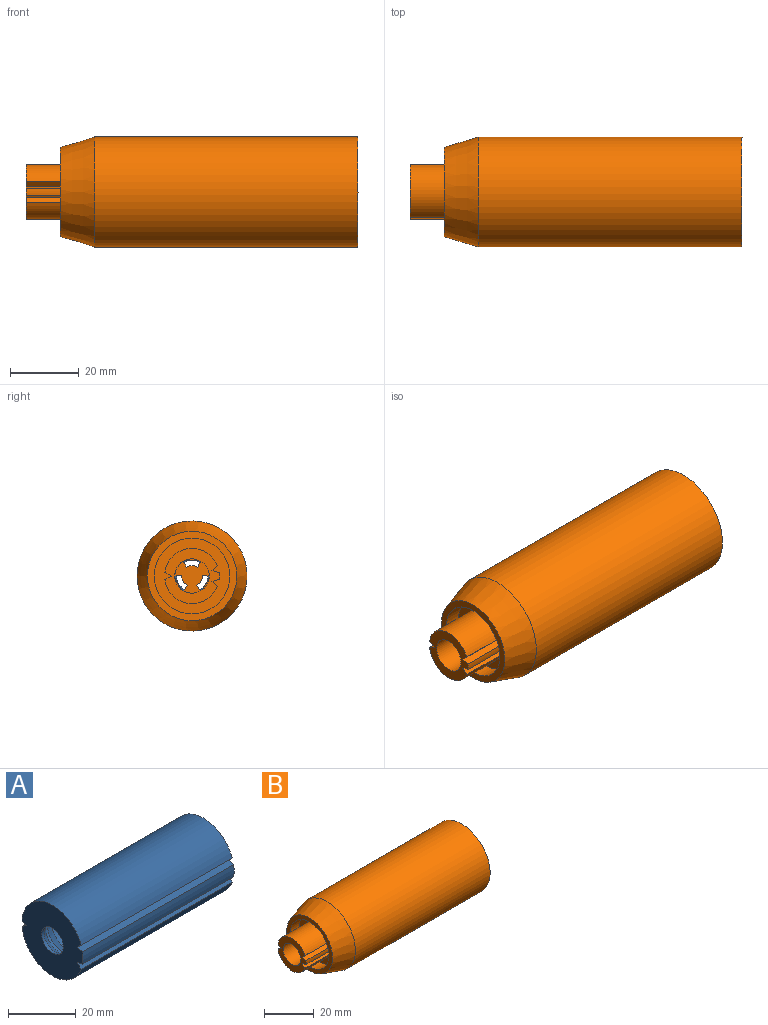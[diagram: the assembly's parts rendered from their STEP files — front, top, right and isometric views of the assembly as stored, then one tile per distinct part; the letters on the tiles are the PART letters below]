
ASSEMBLY  parts=2 mates=1
PART A: 27 faces, bbox 63x25.5x25.5 mm
  f0: cylinder r=9.75mm len=54.43mm, axis (-1,0,0), area 3310.2mm2, adj f3,f4,f18,f19,f20,f21,f22,f23
  f1: cylinder r=12.75mm len=63mm, axis (-1,0,0), area 2171.1mm2, adj f3,f9,f11,f15
  f2: cylinder r=12.75mm len=63mm, axis (-1,0,0), area 2171.1mm2, adj f3,f9,f14,f16
  f3: plane 25.5x25.45mm, normal (1,0,0), area 205.2mm2, adj f0,f1,f2,f10,f11,f12,f13,f14
  f4: cone r=7.25mm half-angle=35deg, axis (1,0,0), area 232.8mm2, adj f0,f5
  f5: cylinder r=7.25mm len=14.5mm, axis (-1,0,0), area 91.1mm2, adj f4,f6
  f6: plane 14.5x14.5mm, normal (1,0,0), area 55.8mm2, adj f5,f7
  f7: cone r=4.5mm half-angle=35deg, axis (1,0,0), area 79.8mm2, adj f6,f8
  f8: cylinder r=4.5mm len=9mm, axis (-1,0,0), area 28.3mm2, adj f7,f9
  f9: plane 25.5x25.45mm, normal (-1,0,0), area 440.3mm2, adj f1,f2,f8,f10,f11,f12,f13,f14
  f10: cylinder r=12.75mm len=63mm, axis (-1,0,0), area 278.5mm2, adj f3,f9,f12,f13
  f11: plane 63x1.59mm, normal (0,-0.71,-0.71), area 141.9mm2, adj f1,f3,f9,f12
  f12: plane 63x2.18mm, normal (0,-0.26,0.97), area 141.9mm2, adj f3,f9,f10,f11
  f13: plane 63x2.18mm, normal (0,-0.26,-0.97), area 141.9mm2, adj f3,f9,f10,f14
  f14: plane 63x1.59mm, normal (0,-0.71,0.71), area 141.9mm2, adj f2,f3,f9,f13
  f15: plane 63x1.95mm, normal (0,0.5,-0.87), area 141.9mm2, adj f1,f3,f9,f16
  f16: plane 63x1.95mm, normal (0,0.5,0.87), area 141.9mm2, adj f2,f3,f9,f15
  f17: plane 4x3mm, normal (0,0,-1), area 12mm2, adj f18,f19,f20,f21
  f18: plane 4x1.21mm, normal (-1,0,0), area 4.3mm2, adj f0,f17,f19,f21
  f19: plane 3x1.21mm, normal (0,1,0), area 3.6mm2, adj f0,f17,f18,f20
  f20: plane 4x1.21mm, normal (1,0,0), area 4.3mm2, adj f0,f17,f19,f21
  f21: plane 3x1.21mm, normal (0,-1,0), area 3.6mm2, adj f0,f17,f18,f20
  f22: plane 3x1.21mm, normal (0,-1,0), area 3.6mm2, adj f0,f23,f25,f26
  f23: plane 4x1.21mm, normal (1,0,0), area 4.3mm2, adj f0,f22,f24,f26
  f24: plane 3x1.21mm, normal (0,1,0), area 3.6mm2, adj f0,f23,f25,f26
  f25: plane 4x1.21mm, normal (-1,0,0), area 4.3mm2, adj f0,f22,f24,f26
  f26: plane 4x3mm, normal (0,0,1), area 12mm2, adj f22,f23,f24,f25
PART B: 52 faces, bbox 96.5x32x32 mm
  f0: plane 16x15.92mm, normal (-1,0,0), area 115.8mm2, adj f1,f2,f3,f15,f46,f47,f48,f49
  f1: cylinder r=8mm len=15.29mm, axis (1,0,0), area 312.2mm2, adj f0,f16,f49,f51
  f2: cylinder r=8mm len=15mm, axis (1,0,0), area 29.4mm2, adj f0,f16,f47,f48
  f3: cylinder r=8mm len=15.29mm, axis (1,0,0), area 312.2mm2, adj f0,f16,f46,f50
  f4: plane 26x25.95mm, normal (1,0,0), area 240.6mm2, adj f5,f6,f7,f12,f40,f41,f42,f43
  f5: cylinder r=13mm len=63.5mm, axis (1,0,0), area 2234mm2, adj f4,f21,f41,f45
  f6: cylinder r=13mm len=63.5mm, axis (1,0,0), area 2234mm2, adj f4,f21,f42,f44
  f7: cylinder r=13mm len=63.5mm, axis (1,0,0), area 289mm2, adj f4,f21,f40,f43
  f8: plane 3.74x0.36mm, normal (-1,0,0), area 0.9mm2, adj f15,f39
  f9: plane 10x9.27mm, normal (-1,0,0), area 52mm2, adj f15,f24,f25,f27,f30,f31,f33,f36
  f10: plane 3.24x1.87mm, normal (-1,0,0), area 0.9mm2, adj f15,f32
  f11: plane 19x19mm, normal (1,0,0), area 230.5mm2, adj f12,f13,f25,f26,f27,f31,f32,f33
  f12: cylinder r=9.5mm len=19mm, axis (1,0,0), area 596.9mm2, adj f4,f11
  f13: cone r=3mm half-angle=26.6deg, axis (-1,0,0), area 63.2mm2, adj f11,f24,f30,f37
  f14: plane 3.24x1.87mm, normal (-1,0,0), area 0.9mm2, adj f15,f26
  f15: cylinder r=5mm len=20mm, axis (1,0,0), area 628.3mm2, adj f0,f8,f9,f10,f14,f22,f23,f28
  f16: plane 22x22mm, normal (-1,0,0), area 185.8mm2, adj f1,f2,f3,f17,f46,f47,f48,f49
  f17: cylinder r=11mm len=22mm, axis (1,0,0), area 345.6mm2, adj f16,f18
  f18: plane 26x26mm, normal (-1,0,0), area 150.8mm2, adj f17,f19
  f19: cone r=13mm half-angle=16.7deg, axis (1,0,0), area 951.2mm2, adj f18,f20
  f20: cylinder r=16mm len=76.5mm, axis (1,0,0), area 7690.6mm2, adj f19,f21
  f21: plane 32x32mm, normal (1,0,0), area 280.1mm2, adj f5,f6,f7,f20,f40,f41,f42,f43
  f22: plane 0.82x0.68mm, normal (1,0,0), area 0.2mm2, adj f15,f25,f26
  f23: plane 0.82x0.47mm, normal (1,0,0), area 0.2mm2, adj f15,f26,f27
  f24: cylinder r=3mm len=3mm, axis (1,0,0), area 10.1mm2, adj f9,f13,f25,f27
  f25: plane 3x2.1mm, normal (0,0.87,0.5), area 7.3mm2, adj f9,f11,f22,f24,f26
  f26: plane 4.87x3mm, normal (0,-0.87,0.5), area 16.9mm2, adj f11,f14,f22,f23,f25,f27
  f27: plane 3x2.43mm, normal (0,0,-1), area 7.3mm2, adj f9,f11,f23,f24,f26
  f28: plane 0.82x0.47mm, normal (1,0,0), area 0.2mm2, adj f15,f31,f32
  f29: plane 0.82x0.68mm, normal (1,0,0), area 0.2mm2, adj f15,f32,f33
  f30: cylinder r=3mm len=3mm, axis (1,0,0), area 10.1mm2, adj f9,f13,f31,f33
  f31: plane 3x2.43mm, normal (0,0,-1), area 7.3mm2, adj f9,f11,f28,f30,f32
  f32: plane 4.87x3mm, normal (0,0.87,0.5), area 16.9mm2, adj f10,f11,f28,f29,f31,f33
  f33: plane 3x2.1mm, normal (0,-0.87,0.5), area 7.3mm2, adj f9,f11,f29,f30,f32
  f34: plane 0.94x0.37mm, normal (1,0,0), area 0.2mm2, adj f15,f38,f39
  f35: plane 0.94x0.37mm, normal (1,0,0), area 0.2mm2, adj f15,f36,f39
  f36: plane 3x2.1mm, normal (0,0.87,0.5), area 7.3mm2, adj f9,f11,f35,f37,f39
  f37: cylinder r=3mm len=3.2mm, axis (1,0,0), area 10.1mm2, adj f9,f13,f36,f38
  f38: plane 3x2.1mm, normal (0,-0.87,0.5), area 7.3mm2, adj f9,f11,f34,f37,f39
  f39: plane 5.63x3mm, normal (0,0,-1), area 16.9mm2, adj f8,f11,f34,f35,f36,f38
  f40: plane 63.5x2.18mm, normal (0,0.26,0.97), area 143.1mm2, adj f4,f7,f21,f41
  f41: plane 63.5x1.59mm, normal (0,0.71,-0.71), area 143.1mm2, adj f4,f5,f21,f40
  f42: plane 63.5x1.59mm, normal (0,0.71,0.71), area 143.1mm2, adj f4,f6,f21,f43
  f43: plane 63.5x2.18mm, normal (0,0.26,-0.97), area 143.1mm2, adj f4,f7,f21,f42
  f44: plane 63.5x1.95mm, normal (0,-0.5,0.87), area 143.1mm2, adj f4,f6,f21,f45
  f45: plane 63.5x1.95mm, normal (0,-0.5,-0.87), area 143.1mm2, adj f4,f5,f21,f44
  f46: plane 15x1.57mm, normal (0,-0.71,-0.71), area 33.3mm2, adj f0,f3,f16,f47
  f47: plane 15x2.14mm, normal (0,-0.26,0.97), area 33.3mm2, adj f0,f2,f16,f46
  f48: plane 15x2.14mm, normal (0,-0.26,-0.97), area 33.3mm2, adj f0,f2,f16,f49
  f49: plane 15x1.57mm, normal (0,-0.71,0.71), area 33.3mm2, adj f0,f1,f16,f48
  f50: plane 15x1.92mm, normal (0,0.5,-0.87), area 33.3mm2, adj f0,f3,f16,f51
  f51: plane 15x1.92mm, normal (0,0.5,0.87), area 33.3mm2, adj f0,f1,f16,f50
PLACE A t=(-16.67,4.52,14.24)mm
PLACE B t=(-20.18,4.58,14.24)mm
MATE fastened A.f9 <-> B.f19  axis (-1,0,0) through (-48.17,4.58,14.24)mm
